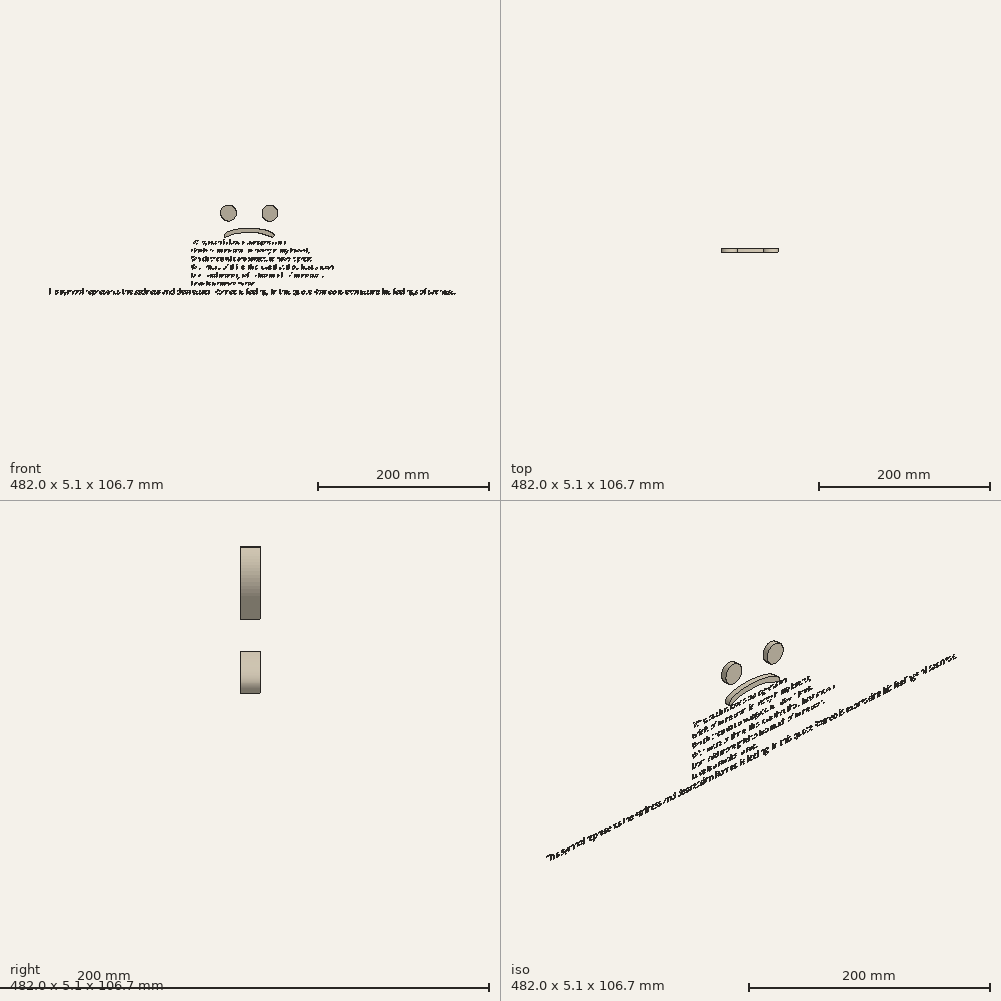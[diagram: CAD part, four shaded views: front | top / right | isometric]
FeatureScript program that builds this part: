
annotation { "Feature Type Name" : "Feature", "Feature Type Description" : "" }
export const myFeature = defineFeature(function(context is Context, id is Id, definition is map)
    precondition{}
    {
        {
            var Q0;
            Q0=qCreatedBy(makeId("Front.planeOp"),FACE);
            var sketch = newSketch(context, id + "F0", { "sketchPlane" : qUnion([Q0])});
            skCircle(sketch, "E0", {"center": v(-24.31, 31.65) * mm, "radius": 9.4 * mm});
            skCircle(sketch, "E1", {"center": v(24.31, 31.43) * mm, "radius": 9.4 * mm});
            skLineSegment(sketch, "E2", {"start": v(-24.31, 31.65) * mm, "end": v(0, 31.65) * mm});
            skLineSegment(sketch, "E3", {"start": v(0, 31.65) * mm, "end": v(24.31, 31.43) * mm});
            skEllipse(sketch, "E4", {"center": v(0, 5.01) * mm, "majorRadius": 29.34 * mm, "minorRadius": 8.83 * mm, "majorAxis": v(1, 0)});
            skPoint(sketch, "E5.5.internal.snap0", {"position": v(-29.34, 5.01) * mm});
            skFitSpline(sketch, "E5", {"points": [v(-28.36, 2.75) * mm, v(-19.64, 6.54) * mm, v(-12.65, 8.04) * mm, v(-2.75, 8.7) * mm, v(10.84, 8.3) * mm, v(22.14, 5.01) * mm, v(28.37, 2.76) * mm], "startDerivative": vector(54.21, 25.95) * mm, "endDerivative": vector(41.82, -15.03) * mm});
            skSolve(sketch);
        }
        {
            var Q0;
            {var subQ0=sQuery(id+"F0.wireOp",EDGE,"E5");Q0=makeQuery(id+"F0.imprint","IMPRINT",FACE,{"disambiguationData":[TD([[makeQuery(id+"F0.imprint","IMPRINT",EDGE,{"derivedFrom":subQ0}),1.0]])]});}
            var Q1;
            Q1=makeQuery(id+"F0.imprint","IMPRINT",FACE,{"disambiguationData":[TD([[makeQuery(id+"F0.imprint","IMPRINT",EDGE,{"derivedFrom":sQuery(id+"F0.wireOp",EDGE,"E0")}),1.0]])]});
            var Q2;
            Q2=makeQuery(id+"F0.imprint","IMPRINT",FACE,{"disambiguationData":[TD([[makeQuery(id+"F0.imprint","IMPRINT",EDGE,{"derivedFrom":sQuery(id+"F0.wireOp",EDGE,"E1")}),1.0]])]});
            extrude(context, id + "F1", {"entities" : qUnion([Q0, Q1, Q2]), "depth" : 5.08 * mm, "offsetDistance" : 25.4 * mm});
        }
        {
            var Q0;
            Q0=qCreatedBy(makeId("Front.planeOp"),FACE);
            var sketch = newSketch(context, id + "F2", { "sketchPlane" : qUnion([Q0])});
            skText(sketch, "E6", { "text": " Why, such is love\'s transgression. \nGriefs of mine own lie heavy in my breast, \nWhich thou wilt propagate, to have it prest \nWith more of thine: this love that thou hast shown \nDoth add more grief to too much of mine own. \nLove is a smoke raised... ", "fontName": "OpenSans-Regular.ttf"});
            const initialGuessF2  = {"E6": [-0.06821, -0.00516, 1, 0, 0.00516]};
            skSetInitialGuess(sketch, initialGuessF2);
            skSolve(sketch);
        }
        {
            var Q0;
            Q0=qCreatedBy(makeId("Front.planeOp"),FACE);
            var sketch = newSketch(context, id + "F3", { "sketchPlane" : qUnion([Q0])});
            skText(sketch, "E7", { "text": "This symbol represents the sadness and depression Romeo is feeling. In this quote Romeo is expressing his feelings of sadness. ", "fontName": "OpenSans-Regular.ttf"});
            const initialGuessF3  = {"E7": [-0.2397, -0.06364, 1, 0, 0.00586]};
            skSetInitialGuess(sketch, initialGuessF3);
            skSolve(sketch);
        }
        {
            var Q0;
            Q0 = qSketchRegion(id + "F2", true);
            var Q1;
            Q1 = qSketchRegion(id + "F3", true);
            extrude(context, id + "F4", {"entities" : qUnion([Q0, Q1]), "depth" : 0.05 * mm, "offsetDistance" : 25.4 * mm});
        }
    });
